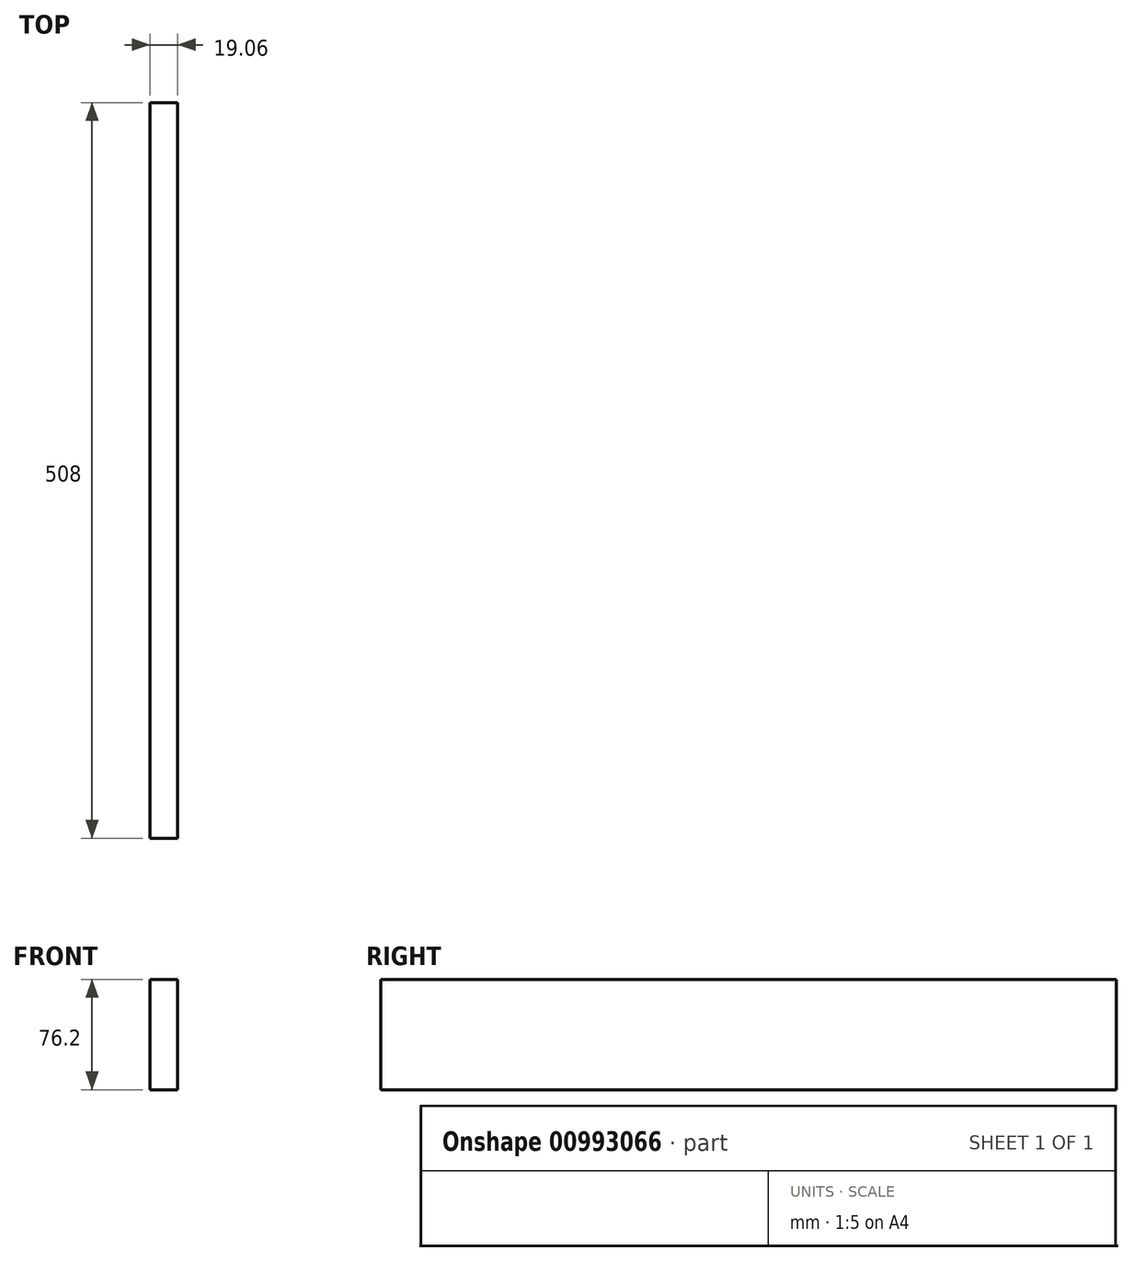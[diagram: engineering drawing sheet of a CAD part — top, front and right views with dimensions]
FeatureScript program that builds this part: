
annotation { "Feature Type Name" : "Feature", "Feature Type Description" : "" }
export const myFeature = defineFeature(function(context is Context, id is Id, definition is map)
    precondition{}
    {
        {
            var Q0;
            Q0=qCreatedBy(makeId("Front.planeOp"),FACE);
            var sketch = newSketch(context, id + "F0", { "sketchPlane" : qUnion([Q0])});
            skLineSegment(sketch, "E0.bottom", {"start": v(-9.53, 38.1) * mm, "end": v(9.53, 38.1) * mm});
            skLineSegment(sketch, "E0.top", {"start": v(-9.53, -38.1) * mm, "end": v(9.53, -38.1) * mm});
            skLineSegment(sketch, "E0.left", {"start": v(-9.53, 38.1) * mm, "end": v(-9.53, -38.1) * mm});
            skLineSegment(sketch, "E0.right", {"start": v(9.53, 38.1) * mm, "end": v(9.53, -38.1) * mm});
            skSolve(sketch);
        }
        {
            var Q0;
            Q0 = qSketchRegion(id + "F0", true);
            extrude(context, id + "F1", {"entities" : qUnion([Q0]), "endBound" : BoundingType.SYMMETRIC, "depth" : 508 * mm, "offsetDistance" : 25.4 * mm});
        }
    });
